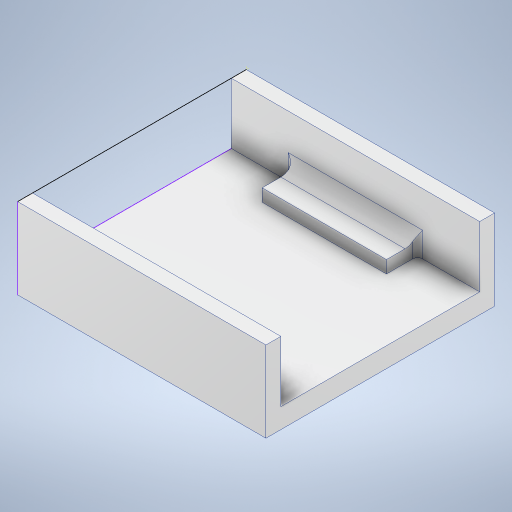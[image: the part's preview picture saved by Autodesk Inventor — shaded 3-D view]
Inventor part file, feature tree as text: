
AUTODESK INVENTOR PART (.ipt)
format: ipt  version: 2024 (Build 280153000, 153)  size: 306,176 bytes
history: native  units: mm
features: sketch x5, extrude x4, fillet x2, projected_geometry x1
ambient origin geometry x8: Origin, YZ Plane, XZ Plane, XY Plane, X Axis, Y Axis, Z Axis, Center Point
bodies: Solid1 (feature_tree)
feature tree (12):
  extrude  "Extrusion1"  Depth=200.0mm
  extrude  "Extrusion2"  Depth=60.0mm
  extrude  "Extrusion3"  Depth=12.0mm
  extrude  "Extrusion6"  Depth=10.0mm TaperAngle=0.0deg
  fillet  "Fillet1"  Radius=12.0mm
  fillet  "Fillet2"  Radius=25.0mm
  sketch  "Sketch8"  dims[d19=25.0mm d20=50.0mm d21=50.0mm d22=50.0mm d23=50.0mm d24=10.0mm d25=0.0mm d26=4.0mm d27=10.0mm]
  sketch  "Sketch1"  dims[d0=160.0mm d1=200.0mm]
  sketch  "Sketch2"  dims[d2=11.0mm d3=0.0mm d4=60.0mm]
  sketch  "Sketch3"  dims[d5=60.0mm d6=12.0mm]
  projected_geometry  "Projected Loop1"
  sketch  "Sketch7"  dims[d7=10.0mm d8=0.0mm d9=5.0mm d10=0.0mm d17=12.0mm d18=25.0mm]
